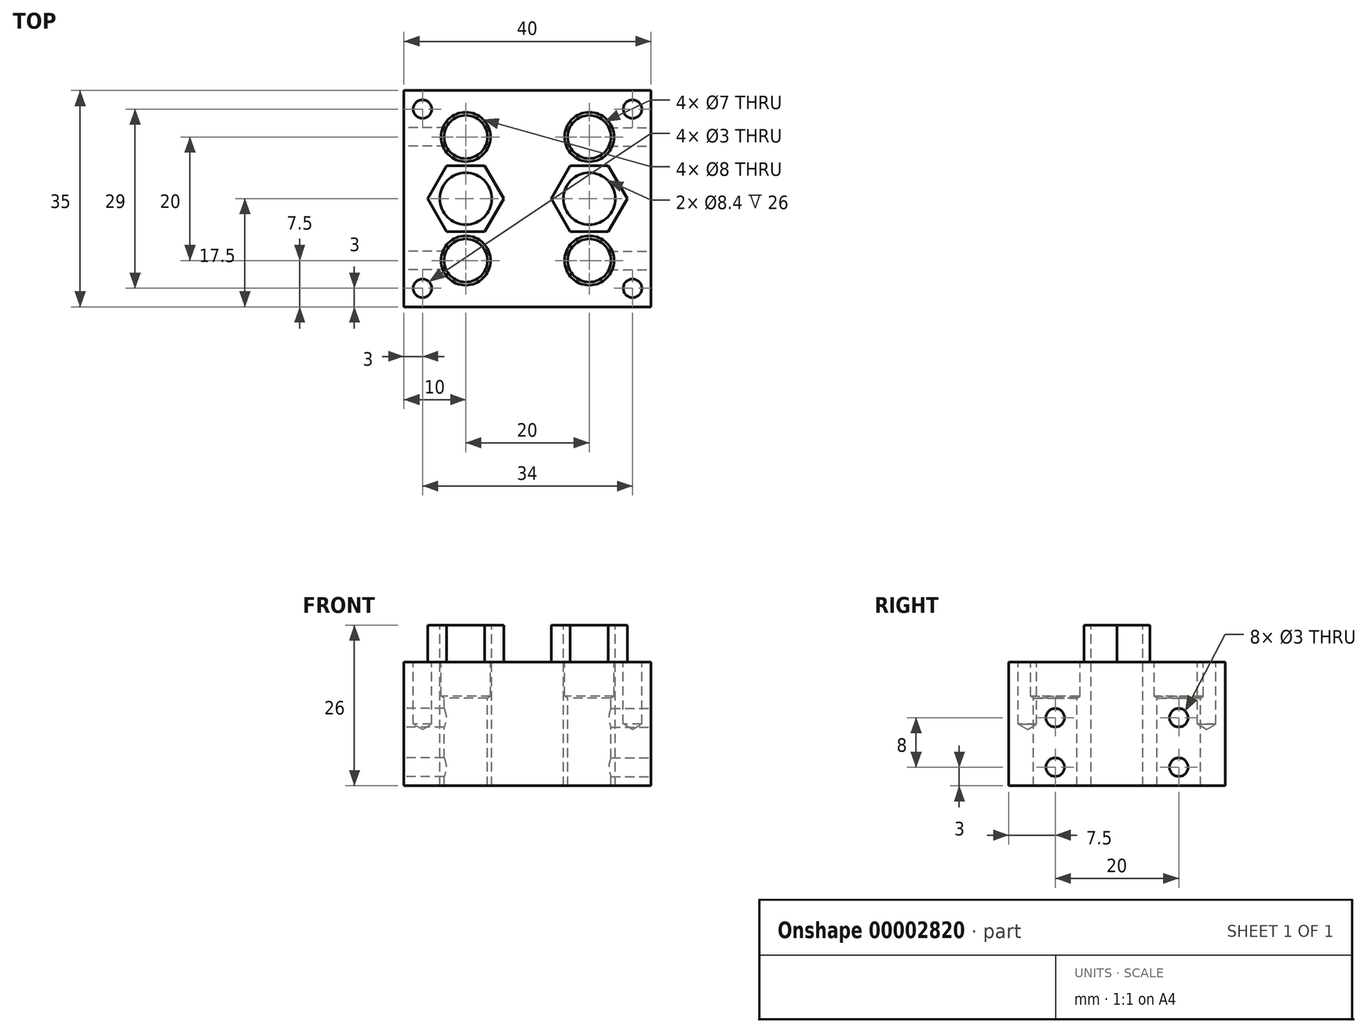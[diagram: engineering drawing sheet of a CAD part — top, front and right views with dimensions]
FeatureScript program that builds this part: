
annotation { "Feature Type Name" : "Feature", "Feature Type Description" : "" }
export const myFeature = defineFeature(function(context is Context, id is Id, definition is map)
    precondition{}
    {
        {
            var Q0;
            Q0=qCreatedBy(makeId("Top.planeOp"),FACE);
            var sketch = newSketch(context, id + "F0", { "sketchPlane" : qUnion([Q0])});
            skLineSegment(sketch, "E0.rect.bottom", {"start": v(-20, 17.5) * mm, "end": v(20, 17.5) * mm});
            skLineSegment(sketch, "E0.rect.top", {"start": v(-20, -17.5) * mm, "end": v(20, -17.5) * mm});
            skLineSegment(sketch, "E0.rect.left", {"start": v(-20, 17.5) * mm, "end": v(-20, -17.5) * mm});
            skLineSegment(sketch, "E0.rect.right", {"start": v(20, 17.5) * mm, "end": v(20, -17.5) * mm});
            skPoint(sketch, "E0.rect.middle", {"position": v(0, 0) * mm});
            skPoint(sketch, "E1", {"position": v(-17, 14.5) * mm});
            skPoint(sketch, "E2", {"position": v(17, 14.5) * mm});
            skPoint(sketch, "E3", {"position": v(17, -14.5) * mm});
            skPoint(sketch, "E4", {"position": v(-17, -14.5) * mm});
            skSolve(sketch);
        }
        {
            var Q0;
            Q0 = qSketchRegion(id + "F0", true);
            extrude(context, id + "F1", {"entities" : qUnion([Q0]), "depth" : 20 * mm});
        }
        {
            var Q0;
            Q0=makeQuery(id+"F1.opExtrude","CAP_FACE",FACE,{"disambiguationData":[OSD([sQuery(id+"F0.wireOp",EDGE,"E0.rect.bottom"),sQuery(id+"F0.wireOp",EDGE,"E0.rect.top"),sQuery(id+"F0.wireOp",EDGE,"E0.rect.left"),sQuery(id+"F0.wireOp",EDGE,"E0.rect.right")])],"isStart":false});
            var sketch = newSketch(context, id + "F2", { "sketchPlane" : qUnion([Q0])});
            skPoint(sketch, "E5.0", {"position": v(-17, 14.5) * mm});
            skPoint(sketch, "E6.0", {"position": v(17, 14.5) * mm});
            skPoint(sketch, "E7.0", {"position": v(17, -14.5) * mm});
            skPoint(sketch, "E8.0", {"position": v(-17, -14.5) * mm});
            skSolve(sketch);
        }
        {
            var Q0;
            Q0=sQuery(id+"F2.wireOp",VERTEX,"E5.0");
            var Q1;
            Q1=sQuery(id+"F2.wireOp",VERTEX,"E6.0");
            var Q2;
            Q2=sQuery(id+"F2.wireOp",VERTEX,"E7.0");
            var Q3;
            Q3=sQuery(id+"F2.wireOp",VERTEX,"E8.0");
            var Q4;
            Q4=makeQuery(id+"F1.opExtrude","SWEPT_BODY",BODY,{"disambiguationData":[OSD([sQuery(id+"F0.wireOp",EDGE,"E0.rect.bottom"),sQuery(id+"F0.wireOp",EDGE,"E0.rect.top"),sQuery(id+"F0.wireOp",EDGE,"E0.rect.left"),sQuery(id+"F0.wireOp",EDGE,"E0.rect.right")])]});
            hole(context, id + "F3", {"style" : HoleStyle.SIMPLE, "holeDiameter" : 3 * mm, "endStyle" : HoleEndStyle.BLIND, "holeDepth" : 10 * mm, "locations" : qUnion([Q0, Q1, Q2, Q3]), "scope" : qUnion([Q4])});
        }
        {
            var Q0;
            Q0=makeQuery(id+"F1.opExtrude","CAP_FACE",FACE,{"disambiguationData":[OSD([sQuery(id+"F0.wireOp",EDGE,"E0.rect.bottom"),sQuery(id+"F0.wireOp",EDGE,"E0.rect.top"),sQuery(id+"F0.wireOp",EDGE,"E0.rect.left"),sQuery(id+"F0.wireOp",EDGE,"E0.rect.right")])],"isStart":false});
            var sketch = newSketch(context, id + "F4", { "sketchPlane" : qUnion([Q0])});
            skLineSegment(sketch, "E9.0.0", {"start": v(20, 17.5) * mm, "end": v(-20, 17.5) * mm, "construction": true});
            skLineSegment(sketch, "E9.0.1", {"start": v(-20, 17.5) * mm, "end": v(-20, -17.5) * mm, "construction": true});
            skLineSegment(sketch, "E9.0.2", {"start": v(-20, -17.5) * mm, "end": v(20, -17.5) * mm, "construction": true});
            skLineSegment(sketch, "E9.0.3", {"start": v(20, -17.5) * mm, "end": v(20, 17.5) * mm, "construction": true});
            skLineSegment(sketch, "E10", {"start": v(0, 17.5) * mm, "end": v(0, -17.5) * mm, "construction": true});
            skLineSegment(sketch, "E11.0", {"start": v(-10, 17.5) * mm, "end": v(-10, -17.5) * mm, "construction": true});
            skLineSegment(sketch, "E12.0", {"start": v(10, 17.5) * mm, "end": v(10, -17.5) * mm, "construction": true});
            skPoint(sketch, "E13", {"position": v(-10, -10) * mm});
            skPoint(sketch, "E14", {"position": v(10, -10) * mm});
            skPoint(sketch, "E15", {"position": v(-10, 10) * mm});
            skPoint(sketch, "E16", {"position": v(10, 10) * mm});
            skLineSegment(sketch, "E17", {"start": v(-20, 0) * mm, "end": v(20, 0) * mm, "construction": true});
            skPoint(sketch, "E18", {"position": v(-10, 0) * mm});
            skPoint(sketch, "E19", {"position": v(10, 0) * mm});
            skSolve(sketch);
        }
        {
            var Q0;
            Q0=sQuery(id+"F4.wireOp",VERTEX,"E15");
            var Q1;
            Q1=sQuery(id+"F4.wireOp",VERTEX,"E16");
            var Q2;
            Q2=sQuery(id+"F4.wireOp",VERTEX,"E13");
            var Q3;
            Q3=sQuery(id+"F4.wireOp",VERTEX,"E14");
            var Q4;
            Q4=makeQuery(id+"F1.opExtrude","SWEPT_BODY",BODY,{"disambiguationData":[OSD([sQuery(id+"F0.wireOp",EDGE,"E0.rect.bottom"),sQuery(id+"F0.wireOp",EDGE,"E0.rect.top"),sQuery(id+"F0.wireOp",EDGE,"E0.rect.left"),sQuery(id+"F0.wireOp",EDGE,"E0.rect.right")])]});
            hole(context, id + "F5", {"style" : HoleStyle.SIMPLE, "holeDiameter" : 8 * mm, "endStyle" : HoleEndStyle.BLIND, "holeDepth" : 5.5 * mm, "locations" : qUnion([Q0, Q1, Q2, Q3]), "scope" : qUnion([Q4])});
        }
        {
            var Q0;
            Q0=sQuery(id+"F4.wireOp",VERTEX,"E18");
            var Q1;
            Q1=sQuery(id+"F4.wireOp",VERTEX,"E19");
            var Q2;
            Q2=makeQuery(id+"F1.opExtrude","SWEPT_BODY",BODY,{"disambiguationData":[OSD([sQuery(id+"F0.wireOp",EDGE,"E0.rect.bottom"),sQuery(id+"F0.wireOp",EDGE,"E0.rect.top"),sQuery(id+"F0.wireOp",EDGE,"E0.rect.left"),sQuery(id+"F0.wireOp",EDGE,"E0.rect.right")])]});
            hole(context, id + "F6", {"style" : HoleStyle.SIMPLE, "holeDiameter" : 8.4 * mm, "endStyle" : HoleEndStyle.THROUGH, "locations" : qUnion([Q0, Q1]), "scope" : qUnion([Q2])});
        }
        {
            var Q0;
            Q0=sQuery(id+"F4.wireOp",VERTEX,"E15");
            var Q1;
            Q1=sQuery(id+"F4.wireOp",VERTEX,"E16");
            var Q2;
            Q2=sQuery(id+"F4.wireOp",VERTEX,"E14");
            var Q3;
            Q3=sQuery(id+"F4.wireOp",VERTEX,"E13");
            var Q4;
            Q4=makeQuery(id+"F1.opExtrude","SWEPT_BODY",BODY,{"disambiguationData":[OSD([sQuery(id+"F0.wireOp",EDGE,"E0.rect.bottom"),sQuery(id+"F0.wireOp",EDGE,"E0.rect.top"),sQuery(id+"F0.wireOp",EDGE,"E0.rect.left"),sQuery(id+"F0.wireOp",EDGE,"E0.rect.right")])]});
            hole(context, id + "F7", {"style" : HoleStyle.SIMPLE, "holeDiameter" : 7 * mm, "endStyle" : HoleEndStyle.THROUGH, "locations" : qUnion([Q0, Q1, Q2, Q3]), "scope" : qUnion([Q4])});
        }
        {
            var Q0;
            Q0=makeQuery(id+"F1.opExtrude","SWEPT_FACE",FACE,{"disambiguationData":[OSD([sQuery(id+"F0.wireOp",EDGE,"E0.rect.right")])]});
            var sketch = newSketch(context, id + "F8", { "sketchPlane" : qUnion([Q0])});
            skLineSegment(sketch, "E20", {"start": v(0, 20) * mm, "end": v(0, 0) * mm, "construction": true});
            skLineSegment(sketch, "E21.0", {"start": v(-10, 20) * mm, "end": v(-10, 0) * mm, "construction": true});
            skLineSegment(sketch, "E22.0", {"start": v(10, 20) * mm, "end": v(10, 0) * mm, "construction": true});
            skPoint(sketch, "E23", {"position": v(-10, 11) * mm});
            skPoint(sketch, "E24", {"position": v(10, 11) * mm});
            skPoint(sketch, "E25", {"position": v(-10, 3) * mm});
            skPoint(sketch, "E26", {"position": v(10, 3) * mm});
            skSolve(sketch);
        }
        {
            var Q0;
            Q0=sQuery(id+"F8.wireOp",VERTEX,"E23");
            var Q1;
            Q1=sQuery(id+"F8.wireOp",VERTEX,"E25");
            var Q2;
            Q2=sQuery(id+"F8.wireOp",VERTEX,"E24");
            var Q3;
            Q3=sQuery(id+"F8.wireOp",VERTEX,"E26");
            var Q4;
            Q4=makeQuery(id+"F1.opExtrude","SWEPT_BODY",BODY,{"disambiguationData":[OSD([sQuery(id+"F0.wireOp",EDGE,"E0.rect.bottom"),sQuery(id+"F0.wireOp",EDGE,"E0.rect.top"),sQuery(id+"F0.wireOp",EDGE,"E0.rect.left"),sQuery(id+"F0.wireOp",EDGE,"E0.rect.right")])]});
            hole(context, id + "F9", {"style" : HoleStyle.SIMPLE, "holeDiameter" : 3 * mm, "endStyle" : HoleEndStyle.BLIND, "holeDepth" : 8 * mm, "locations" : qUnion([Q0, Q1, Q2, Q3]), "scope" : qUnion([Q4])});
        }
        {
            var Q0;
            Q0=makeQuery(id+"F1.opExtrude","SWEPT_FACE",FACE,{"disambiguationData":[OSD([sQuery(id+"F0.wireOp",EDGE,"E0.rect.left")])]});
            var sketch = newSketch(context, id + "F10", { "sketchPlane" : qUnion([Q0])});
            skPoint(sketch, "E27.0", {"position": v(-10, 3) * mm});
            skPoint(sketch, "E28.0", {"position": v(-10, 11) * mm});
            skPoint(sketch, "E29.0", {"position": v(10, 11) * mm});
            skPoint(sketch, "E30.0", {"position": v(10, 3) * mm});
            skSolve(sketch);
        }
        {
            var Q0;
            Q0=sQuery(id+"F10.wireOp",VERTEX,"E28.0");
            var Q1;
            Q1=sQuery(id+"F10.wireOp",VERTEX,"E27.0");
            var Q2;
            Q2=sQuery(id+"F10.wireOp",VERTEX,"E29.0");
            var Q3;
            Q3=sQuery(id+"F10.wireOp",VERTEX,"E30.0");
            var Q4;
            Q4=makeQuery(id+"F1.opExtrude","SWEPT_BODY",BODY,{"disambiguationData":[OSD([sQuery(id+"F0.wireOp",EDGE,"E0.rect.bottom"),sQuery(id+"F0.wireOp",EDGE,"E0.rect.top"),sQuery(id+"F0.wireOp",EDGE,"E0.rect.left"),sQuery(id+"F0.wireOp",EDGE,"E0.rect.right")])]});
            hole(context, id + "F11", {"style" : HoleStyle.SIMPLE, "holeDiameter" : 3 * mm, "endStyle" : HoleEndStyle.BLIND, "holeDepth" : 8 * mm, "locations" : qUnion([Q0, Q1, Q2, Q3]), "scope" : qUnion([Q4])});
        }
        {
            var Q0;
            Q0=makeQuery(id+"F1.opExtrude","CAP_FACE",FACE,{"disambiguationData":[OSD([sQuery(id+"F0.wireOp",EDGE,"E0.rect.bottom"),sQuery(id+"F0.wireOp",EDGE,"E0.rect.top"),sQuery(id+"F0.wireOp",EDGE,"E0.rect.left"),sQuery(id+"F0.wireOp",EDGE,"E0.rect.right")])],"isStart":false});
            var sketch = newSketch(context, id + "F12", { "sketchPlane" : qUnion([Q0])});
            skCircle(sketch, "E31.0", {"center": v(-10, 0) * mm, "radius": 4.2 * mm});
            skCircle(sketch, "E32.0", {"center": v(10, 0) * mm, "radius": 4.2 * mm});
            skCircle(sketch, "E33.cCircle", {"center": v(-10, 0) * mm, "radius": 6.17 * mm, "construction": true});
            skLineSegment(sketch, "E33.0", {"start": v(-16.18, 0) * mm, "end": v(-13.09, 5.35) * mm});
            skLineSegment(sketch, "E33.1", {"start": v(-13.09, 5.35) * mm, "end": v(-6.91, 5.35) * mm});
            skLineSegment(sketch, "E33.2", {"start": v(-6.91, 5.35) * mm, "end": v(-3.82, 0) * mm});
            skLineSegment(sketch, "E33.3", {"start": v(-3.83, 0) * mm, "end": v(-6.91, -5.35) * mm});
            skLineSegment(sketch, "E33.4", {"start": v(-6.91, -5.35) * mm, "end": v(-13.09, -5.35) * mm});
            skLineSegment(sketch, "E33.5", {"start": v(-13.09, -5.35) * mm, "end": v(-16.18, 0) * mm});
            skCircle(sketch, "E34.cCircle", {"center": v(10, 0) * mm, "radius": 6.17 * mm, "construction": true});
            skLineSegment(sketch, "E34.0", {"start": v(3.82, 0) * mm, "end": v(6.91, 5.35) * mm});
            skLineSegment(sketch, "E34.1", {"start": v(6.91, 5.35) * mm, "end": v(13.09, 5.35) * mm});
            skLineSegment(sketch, "E34.2", {"start": v(13.09, 5.35) * mm, "end": v(16.18, 0) * mm});
            skLineSegment(sketch, "E34.3", {"start": v(16.18, 0) * mm, "end": v(13.09, -5.35) * mm});
            skLineSegment(sketch, "E34.4", {"start": v(13.09, -5.35) * mm, "end": v(6.91, -5.35) * mm});
            skLineSegment(sketch, "E34.5", {"start": v(6.91, -5.35) * mm, "end": v(3.82, 0) * mm});
            skSolve(sketch);
        }
        {
            var Q0;
            Q0 = qSketchRegion(id + "F12", true);
            extrude(context, id + "F13", {"entities" : qUnion([Q0]), "operationType" : NewBodyOperationType.ADD, "depth" : 6 * mm});
        }
    });
